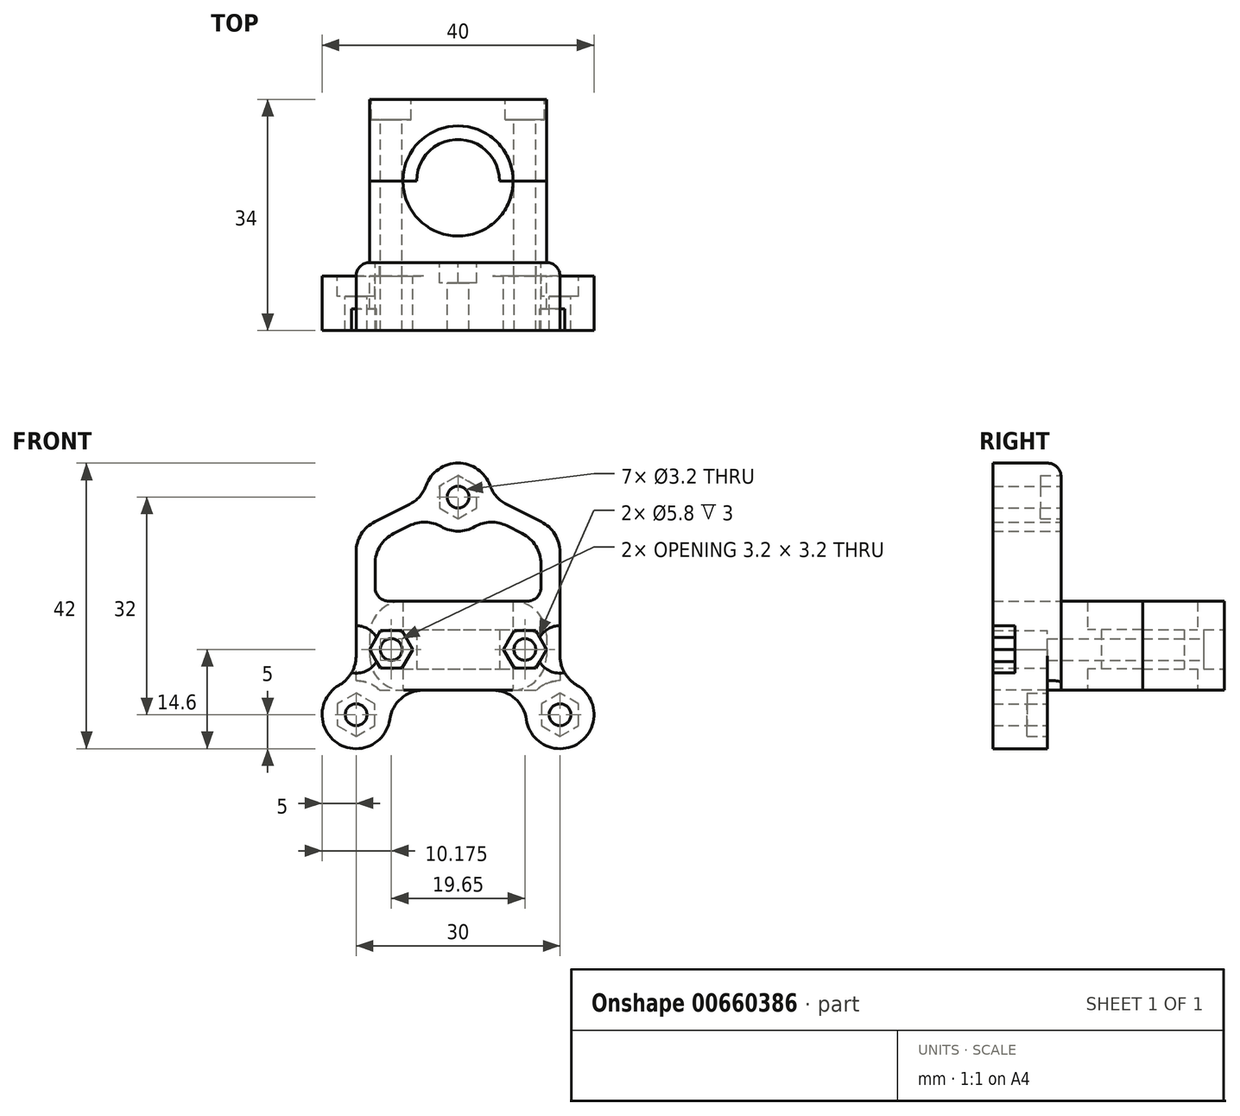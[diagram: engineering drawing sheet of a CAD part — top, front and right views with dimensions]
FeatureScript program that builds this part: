
annotation { "Feature Type Name" : "Feature", "Feature Type Description" : "" }
export const myFeature = defineFeature(function(context is Context, id is Id, definition is map)
    precondition{}
    {
        {
            var Q0;
            Q0=qCreatedBy(makeId("Front.planeOp"),FACE);
            var sketch = newSketch(context, id + "F0", { "sketchPlane" : qUnion([Q0])});
            skCircle(sketch, "E0", {"center": v(0, 0) * mm, "radius": 1.6 * mm});
            skCircle(sketch, "E1", {"center": v(-15, -32) * mm, "radius": 1.6 * mm});
            skCircle(sketch, "E2", {"center": v(15, -32) * mm, "radius": 1.6 * mm});
            skCircle(sketch, "E3", {"center": v(0, 0) * mm, "radius": 5 * mm});
            skCircle(sketch, "E4", {"center": v(-15, -32) * mm, "radius": 5 * mm});
            skCircle(sketch, "E5", {"center": v(15, -32) * mm, "radius": 5 * mm});
            skLineSegment(sketch, "E6", {"start": v(-34.89, -28.4) * mm, "end": v(34.55, -28.4) * mm, "construction": true});
            skLineSegment(sketch, "E7", {"start": v(-36.38, -22.4) * mm, "end": v(39.22, -22.4) * mm, "construction": true});
            skLineSegment(sketch, "E8", {"start": v(-25.23, 0) * mm, "end": v(32.74, 0) * mm, "construction": true});
            skPoint(sketch, "E9", {"position": v(0, -5) * mm});
            skLineSegment(sketch, "E10", {"start": v(-5, 0) * mm, "end": v(-15, -5) * mm});
            skLineSegment(sketch, "E11", {"start": v(5, 0) * mm, "end": v(15, -5) * mm});
            skCircle(sketch, "E12.cCircle", {"center": v(-9.82, -22.4) * mm, "radius": 2.75 * mm, "construction": true});
            skLineSegment(sketch, "E12.0", {"start": v(-8.24, -25.15) * mm, "end": v(-11.41, -25.15) * mm});
            skLineSegment(sketch, "E12.1", {"start": v(-11.41, -25.15) * mm, "end": v(-13, -22.4) * mm});
            skLineSegment(sketch, "E12.2", {"start": v(-13, -22.4) * mm, "end": v(-11.41, -19.65) * mm});
            skLineSegment(sketch, "E12.3", {"start": v(-11.41, -19.65) * mm, "end": v(-8.24, -19.65) * mm});
            skLineSegment(sketch, "E12.4", {"start": v(-8.24, -19.65) * mm, "end": v(-6.65, -22.4) * mm});
            skLineSegment(sketch, "E12.5", {"start": v(-6.65, -22.4) * mm, "end": v(-8.24, -25.15) * mm});
            skPoint(sketch, "E12.0.midPoint", {"position": v(0, -22.4) * mm});
            skLineSegment(sketch, "E13", {"start": v(-15, -5) * mm, "end": v(-15, -27) * mm});
            skLineSegment(sketch, "E14", {"start": v(15, -5) * mm, "end": v(15, -27) * mm});
            skLineSegment(sketch, "E15", {"start": v(-11.53, -28.4) * mm, "end": v(11.53, -28.4) * mm});
            skLineSegment(sketch, "E16", {"start": v(-30.83, -32) * mm, "end": v(25.55, -32) * mm, "construction": true});
            skLineSegment(sketch, "E17", {"start": v(-10, -32) * mm, "end": v(-10, -28.4) * mm});
            skLineSegment(sketch, "E18", {"start": v(10, -32) * mm, "end": v(10, -28.4) * mm});
            skLineSegment(sketch, "E19", {"start": v(-12.2, -15.3) * mm, "end": v(12.2, -15.3) * mm});
            skLineSegment(sketch, "E20.0", {"start": v(-4.2, -2.73) * mm, "end": v(-12.2, -6.73) * mm});
            skLineSegment(sketch, "E21.0", {"start": v(4.2, -2.73) * mm, "end": v(12.2, -6.73) * mm});
            skLineSegment(sketch, "E22", {"start": v(-12.2, -6.73) * mm, "end": v(-12.2, -15.3) * mm});
            skLineSegment(sketch, "E23", {"start": v(12.2, -6.73) * mm, "end": v(12.2, -15.3) * mm});
            skCircle(sketch, "E24.cCircle", {"center": v(9.82, -22.4) * mm, "radius": 2.75 * mm, "construction": true});
            skLineSegment(sketch, "E24.0", {"start": v(11.41, -25.15) * mm, "end": v(8.24, -25.15) * mm});
            skLineSegment(sketch, "E24.1", {"start": v(8.24, -25.15) * mm, "end": v(6.65, -22.4) * mm});
            skLineSegment(sketch, "E24.2", {"start": v(6.65, -22.4) * mm, "end": v(8.24, -19.65) * mm});
            skLineSegment(sketch, "E24.3", {"start": v(8.24, -19.65) * mm, "end": v(11.41, -19.65) * mm});
            skLineSegment(sketch, "E24.4", {"start": v(11.41, -19.65) * mm, "end": v(13, -22.4) * mm});
            skLineSegment(sketch, "E24.5", {"start": v(13, -22.4) * mm, "end": v(11.41, -25.15) * mm});
            skCircle(sketch, "E25", {"center": v(-15, -22.4) * mm, "radius": 3.5 * mm});
            skCircle(sketch, "E26", {"center": v(15, -22.4) * mm, "radius": 3.5 * mm});
            skLineSegment(sketch, "E27.bottom", {"start": v(-3.5, -14.5) * mm, "end": v(3.5, -14.5) * mm, "construction": true});
            skLineSegment(sketch, "E27.top", {"start": v(-3.5, -15.7) * mm, "end": v(3.5, -15.7) * mm, "construction": true});
            skLineSegment(sketch, "E27.left", {"start": v(-3.5, -14.5) * mm, "end": v(-3.5, -15.7) * mm, "construction": true});
            skLineSegment(sketch, "E27.right", {"start": v(3.5, -14.5) * mm, "end": v(3.5, -15.7) * mm, "construction": true});
            skPoint(sketch, "E28", {"position": v(0, -14.5) * mm});
            skLineSegment(sketch, "E29.bottom", {"start": v(-8, -15.7) * mm, "end": v(8, -15.7) * mm, "construction": true});
            skLineSegment(sketch, "E29.top", {"start": v(-8, -19.4) * mm, "end": v(8, -19.4) * mm, "construction": true});
            skLineSegment(sketch, "E29.left", {"start": v(-8, -15.7) * mm, "end": v(-8, -19.4) * mm, "construction": true});
            skLineSegment(sketch, "E29.right", {"start": v(8, -15.7) * mm, "end": v(8, -19.4) * mm, "construction": true});
            skLineSegment(sketch, "E30.bottom", {"start": v(-8, -25.4) * mm, "end": v(8, -25.4) * mm, "construction": true});
            skLineSegment(sketch, "E30.top", {"start": v(-8, -28.4) * mm, "end": v(8, -28.4) * mm, "construction": true});
            skLineSegment(sketch, "E30.left", {"start": v(-8, -25.4) * mm, "end": v(-8, -28.4) * mm, "construction": true});
            skLineSegment(sketch, "E30.right", {"start": v(8, -25.4) * mm, "end": v(8, -28.4) * mm, "construction": true});
            skLineSegment(sketch, "E31.bottom", {"start": v(-6, -19.4) * mm, "end": v(6, -19.4) * mm, "construction": true});
            skLineSegment(sketch, "E31.top", {"start": v(-6, -25.4) * mm, "end": v(6, -25.4) * mm, "construction": true});
            skLineSegment(sketch, "E31.left", {"start": v(-6, -19.4) * mm, "end": v(-6, -25.4) * mm, "construction": true});
            skLineSegment(sketch, "E31.right", {"start": v(6, -19.4) * mm, "end": v(6, -25.4) * mm, "construction": true});
            skLineSegment(sketch, "E32.bottom", {"start": v(-5, -28.4) * mm, "end": v(5, -28.4) * mm, "construction": true});
            skLineSegment(sketch, "E33", {"start": v(0, -14.5) * mm, "end": v(0, -28.4) * mm, "construction": true});
            skLineSegment(sketch, "E34", {"start": v(-13, -2.8) * mm, "end": v(-13, -40.8) * mm, "construction": true});
            skLineSegment(sketch, "E35", {"start": v(13, -2.8) * mm, "end": v(13, -40.8) * mm, "construction": true});
            skPoint(sketch, "E36", {"position": v(-8, -23.4) * mm});
            skPoint(sketch, "E37", {"position": v(8, -23.4) * mm});
            skArc(sketch, "E38", {"start": v(-8, -15.3) * mm, "mid": v(-11.54, -16.76) * mm, "end": v(-13, -20.3) * mm, "construction": true});
            skArc(sketch, "E39", {"start": v(8, -15.3) * mm, "mid": v(11.54, -16.76) * mm, "end": v(13, -20.3) * mm, "construction": true});
            skArc(sketch, "E40", {"start": v(-8, -28.4) * mm, "mid": v(-11.54, -26.94) * mm, "end": v(-13, -23.4) * mm, "construction": true});
            skArc(sketch, "E41", {"start": v(8, -28.4) * mm, "mid": v(11.54, -26.94) * mm, "end": v(13, -23.4) * mm, "construction": true});
            skSolve(sketch);
        }
        {
            var Q0;
            {var subQ18=sQuery(id+"F0.wireOp",EDGE,"E10");Q0=makeQuery(id+"F0.imprint","IMPRINT",FACE,{"disambiguationData":[TD([[makeQuery(id+"F0.imprint","IMPRINT",EDGE,{"derivedFrom":subQ18}),1.0]])]});}
            var Q1;
            Q1=makeQuery(id+"F0.imprint","IMPRINT",FACE,{"disambiguationData":[TD([[makeQuery(id+"F0.imprint","IMPRINT",EDGE,{"derivedFrom":sQuery(id+"F0.wireOp",EDGE,"E1")}),-1.0]])]});
            var Q2;
            {var subQ3=sQuery(id+"F0.wireOp",EDGE,"E17");Q2=makeQuery(id+"F0.imprint","IMPRINT",FACE,{"disambiguationData":[TD([[makeQuery(id+"F0.imprint","IMPRINT",EDGE,{"derivedFrom":subQ3}),1.0]])]});}
            var Q3;
            Q3=makeQuery(id+"F0.imprint","IMPRINT",FACE,{"disambiguationData":[TD([[makeQuery(id+"F0.imprint","IMPRINT",EDGE,{"derivedFrom":sQuery(id+"F0.wireOp",EDGE,"E2")}),-1.0]])]});
            var Q4;
            {var subQ3=sQuery(id+"F0.wireOp",EDGE,"E18");Q4=makeQuery(id+"F0.imprint","IMPRINT",FACE,{"disambiguationData":[TD([[makeQuery(id+"F0.imprint","IMPRINT",EDGE,{"derivedFrom":subQ3}),-1.0]])]});}
            var Q5;
            Q5=makeQuery(id+"F0.imprint","IMPRINT",FACE,{"disambiguationData":[TD([[makeQuery(id+"F0.imprint","IMPRINT",EDGE,{"derivedFrom":sQuery(id+"F0.wireOp",EDGE,"E0")}),-1.0]])]});
            extrude(context, id + "F1", {"entities" : qUnion([Q0, Q1, Q2, Q3, Q4, Q5]), "oppositeDirection" : true, "depth" : -22 * mm, "offsetDistance" : 25 * mm, "hasSecondDirection" : true, "secondDirectionOppositeDirection" : true, "secondDirectionDepth" : -18.8 * mm});
        }
        {
            var Q0;
            Q0=makeQuery(id+"F0.imprint","IMPRINT",FACE,{"disambiguationData":[TD([[makeQuery(id+"F0.imprint","IMPRINT",EDGE,{"derivedFrom":sQuery(id+"F0.wireOp",EDGE,"E1")}),-1.0]])]});
            var Q1;
            {var subQ3=sQuery(id+"F0.wireOp",EDGE,"E17");Q1=makeQuery(id+"F0.imprint","IMPRINT",FACE,{"disambiguationData":[TD([[makeQuery(id+"F0.imprint","IMPRINT",EDGE,{"derivedFrom":subQ3}),1.0]])]});}
            var Q2;
            {var subQ4=sQuery(id+"F0.wireOp",EDGE,"E12.2");var subQ5=sQuery(id+"F0.wireOp",EDGE,"E12.1");var subQ6=makeQuery(id+"F0.imprint","INTERSECT",VERTEX,{"derivedFrom":[subQ5,subQ4]});Q2=makeQuery(id+"F0.imprint","IMPRINT",FACE,{"disambiguationData":[TD([[makeQuery(id+"F0.imprint","IMPRINT",EDGE,{"disambiguationData":[TD([[subQ6,1.0]])],"derivedFrom":subQ5}),1.0]])]});}
            var Q3;
            Q3=makeQuery(id+"F0.imprint","IMPRINT",FACE,{"disambiguationData":[TD([[makeQuery(id+"F0.imprint","IMPRINT",EDGE,{"derivedFrom":sQuery(id+"F0.wireOp",EDGE,"E0")}),-1.0]])]});
            var Q4;
            {var subQ0=sQuery(id+"F0.wireOp",EDGE,"E26");var subQ1=sQuery(id+"F0.wireOp",EDGE,"E14");var subQ2=makeQuery(id+"F0.imprint","INTERSECT",VERTEX,{"disambiguationData":[OD(0.0)],"derivedFrom":[subQ1,subQ0]});Q4=makeQuery(id+"F0.imprint","IMPRINT",FACE,{"disambiguationData":[TD([[makeQuery(id+"F0.imprint","IMPRINT",EDGE,{"disambiguationData":[TD([[subQ2,-1.0]])],"derivedFrom":subQ1}),-1.0]])]});}
            var Q5;
            {var subQ16=sQuery(id+"F0.wireOp",EDGE,"E10");Q5=makeQuery(id+"F0.imprint","IMPRINT",FACE,{"disambiguationData":[TD([[makeQuery(id+"F0.imprint","IMPRINT",EDGE,{"derivedFrom":subQ16}),1.0]])]});}
            var Q6;
            {var subQ3=sQuery(id+"F0.wireOp",EDGE,"E18");Q6=makeQuery(id+"F0.imprint","IMPRINT",FACE,{"disambiguationData":[TD([[makeQuery(id+"F0.imprint","IMPRINT",EDGE,{"derivedFrom":subQ3}),-1.0]])]});}
            var Q7;
            Q7=makeQuery(id+"F0.imprint","IMPRINT",FACE,{"disambiguationData":[TD([[makeQuery(id+"F0.imprint","IMPRINT",EDGE,{"derivedFrom":sQuery(id+"F0.wireOp",EDGE,"E2")}),-1.0]])]});
            extrude(context, id + "F2", {"entities" : qUnion([Q0, Q1, Q2, Q3, Q4, Q5, Q6, Q7]), "operationType" : NewBodyOperationType.ADD, "oppositeDirection" : true, "depth" : -18.8 * mm, "offsetDistance" : 25 * mm, "hasSecondDirection" : true, "secondDirectionOppositeDirection" : true, "secondDirectionDepth" : -14 * mm});
        }
        {
            var Q0;
            {var subQ16=sQuery(id+"F0.wireOp",EDGE,"E10");Q0=makeQuery(id+"F0.imprint","IMPRINT",FACE,{"disambiguationData":[TD([[makeQuery(id+"F0.imprint","IMPRINT",EDGE,{"derivedFrom":subQ16}),1.0]])]});}
            var Q1;
            {var subQ5=sQuery(id+"F0.wireOp",EDGE,"E12.0");Q1=makeQuery(id+"F0.imprint","IMPRINT",FACE,{"disambiguationData":[TD([[makeQuery(id+"F0.imprint","IMPRINT",EDGE,{"derivedFrom":subQ5}),-1.0]])]});}
            var Q2;
            {var subQ0=sQuery(id+"F0.wireOp",EDGE,"E12.2");var subQ1=sQuery(id+"F0.wireOp",EDGE,"E12.1");var subQ2=makeQuery(id+"F0.imprint","INTERSECT",VERTEX,{"derivedFrom":[subQ1,subQ0]});Q2=makeQuery(id+"F0.imprint","IMPRINT",FACE,{"disambiguationData":[TD([[makeQuery(id+"F0.imprint","IMPRINT",EDGE,{"disambiguationData":[TD([[subQ2,1.0]])],"derivedFrom":subQ1}),-1.0]])]});}
            var Q3;
            {var subQ4=sQuery(id+"F0.wireOp",EDGE,"E12.2");var subQ5=sQuery(id+"F0.wireOp",EDGE,"E12.1");var subQ6=makeQuery(id+"F0.imprint","INTERSECT",VERTEX,{"derivedFrom":[subQ5,subQ4]});Q3=makeQuery(id+"F0.imprint","IMPRINT",FACE,{"disambiguationData":[TD([[makeQuery(id+"F0.imprint","IMPRINT",EDGE,{"disambiguationData":[TD([[subQ6,1.0]])],"derivedFrom":subQ5}),1.0]])]});}
            var Q4;
            {var subQ6=sQuery(id+"F0.wireOp",EDGE,"E24.0");Q4=makeQuery(id+"F0.imprint","IMPRINT",FACE,{"disambiguationData":[TD([[makeQuery(id+"F0.imprint","IMPRINT",EDGE,{"derivedFrom":subQ6}),-1.0]])]});}
            var Q5;
            {var subQ0=sQuery(id+"F0.wireOp",EDGE,"E26");var subQ1=sQuery(id+"F0.wireOp",EDGE,"E14");var subQ2=makeQuery(id+"F0.imprint","INTERSECT",VERTEX,{"disambiguationData":[OD(0.0)],"derivedFrom":[subQ1,subQ0]});Q5=makeQuery(id+"F0.imprint","IMPRINT",FACE,{"disambiguationData":[TD([[makeQuery(id+"F0.imprint","IMPRINT",EDGE,{"disambiguationData":[TD([[subQ2,-1.0]])],"derivedFrom":subQ1}),-1.0]])]});}
            var Q6;
            {var subQ0=sQuery(id+"F0.wireOp",EDGE,"E24.5");var subQ1=sQuery(id+"F0.wireOp",EDGE,"E24.4");var subQ2=makeQuery(id+"F0.imprint","INTERSECT",VERTEX,{"derivedFrom":[subQ1,subQ0]});Q6=makeQuery(id+"F0.imprint","IMPRINT",FACE,{"disambiguationData":[TD([[makeQuery(id+"F0.imprint","IMPRINT",EDGE,{"disambiguationData":[TD([[subQ2,1.0]])],"derivedFrom":subQ1}),-1.0]])]});}
            var Q7;
            Q7=makeQuery(id+"F0.imprint","IMPRINT",FACE,{"disambiguationData":[TD([[makeQuery(id+"F0.imprint","IMPRINT",EDGE,{"derivedFrom":sQuery(id+"F0.wireOp",EDGE,"E0")}),-1.0]])]});
            extrude(context, id + "F3", {"entities" : qUnion([Q0, Q1, Q2, Q3, Q4, Q5, Q6, Q7]), "operationType" : NewBodyOperationType.ADD, "oppositeDirection" : true, "depth" : -14 * mm, "offsetDistance" : 25 * mm, "hasSecondDirection" : true, "secondDirectionOppositeDirection" : true, "secondDirectionDepth" : -12 * mm});
        }
        {
            var Q0;
            Q0=qCreatedBy(makeId("Front.planeOp"),FACE);
            var sketch = newSketch(context, id + "F4", { "sketchPlane" : qUnion([Q0])});
            skPoint(sketch, "E42.0.midPoint", {"position": v(0, -22.4) * mm});
            skArc(sketch, "E43", {"start": v(-8, -15.3) * mm, "mid": v(-11.54, -16.76) * mm, "end": v(-13, -20.3) * mm});
            skArc(sketch, "E44", {"start": v(8, -15.3) * mm, "mid": v(11.54, -16.76) * mm, "end": v(13, -20.3) * mm});
            skArc(sketch, "E45", {"start": v(-8, -28.4) * mm, "mid": v(-11.54, -26.94) * mm, "end": v(-13, -23.4) * mm});
            skArc(sketch, "E46", {"start": v(8, -28.4) * mm, "mid": v(11.54, -26.94) * mm, "end": v(13, -23.4) * mm});
            skLineSegment(sketch, "E47", {"start": v(-13, -20.3) * mm, "end": v(-13, -23.4) * mm});
            skLineSegment(sketch, "E48", {"start": v(-8, -15.3) * mm, "end": v(8, -15.3) * mm});
            skLineSegment(sketch, "E49", {"start": v(13, -20.3) * mm, "end": v(13, -23.4) * mm});
            skLineSegment(sketch, "E50", {"start": v(8, -28.4) * mm, "end": v(-8, -28.4) * mm});
            skPoint(sketch, "E51", {"position": v(-9.82, -22.4) * mm});
            skPoint(sketch, "E52", {"position": v(9.83, -22.4) * mm});
            skSolve(sketch);
        }
        {
            var Q0;
            Q0 = qSketchRegion(id + "F4", true);
            extrude(context, id + "F5", {"entities" : qUnion([Q0]), "operationType" : NewBodyOperationType.ADD, "depth" : 12 * mm, "offsetDistance" : 25 * mm});
        }
        {
            var Q0;
            Q0 = qSketchRegion(id + "F4", true);
            extrude(context, id + "F6", {"entities" : qUnion([Q0]), "oppositeDirection" : true, "depth" : 12 * mm, "offsetDistance" : 25 * mm});
        }
        {
            var Q0;
            Q0=qCreatedBy(makeId("Front.planeOp"),FACE);
            var sketch = newSketch(context, id + "F7", { "sketchPlane" : qUnion([Q0])});
            skLineSegment(sketch, "E53.bottom", {"start": v(-3.5, -14.5) * mm, "end": v(3.5, -14.5) * mm});
            skLineSegment(sketch, "E53.top", {"start": v(-3.5, -15.7) * mm, "end": v(3.5, -15.7) * mm});
            skLineSegment(sketch, "E53.left", {"start": v(-3.5, -14.5) * mm, "end": v(-3.5, -15.7) * mm});
            skLineSegment(sketch, "E53.right", {"start": v(3.5, -14.5) * mm, "end": v(3.5, -15.7) * mm});
            skLineSegment(sketch, "E54.bottom", {"start": v(-8, -15.7) * mm, "end": v(8, -15.7) * mm});
            skLineSegment(sketch, "E54.top", {"start": v(-8, -19.4) * mm, "end": v(8, -19.4) * mm});
            skLineSegment(sketch, "E54.left", {"start": v(-8, -15.7) * mm, "end": v(-8, -19.4) * mm});
            skLineSegment(sketch, "E54.right", {"start": v(8, -15.7) * mm, "end": v(8, -19.4) * mm});
            skLineSegment(sketch, "E55.bottom", {"start": v(-8, -25.4) * mm, "end": v(8, -25.4) * mm});
            skLineSegment(sketch, "E55.top", {"start": v(-8, -28.4) * mm, "end": v(8, -28.4) * mm});
            skLineSegment(sketch, "E55.left", {"start": v(-8, -25.4) * mm, "end": v(-8, -28.4) * mm});
            skLineSegment(sketch, "E55.right", {"start": v(8, -25.4) * mm, "end": v(8, -28.4) * mm});
            skLineSegment(sketch, "E56.bottom", {"start": v(-6, -19.4) * mm, "end": v(6, -19.4) * mm});
            skLineSegment(sketch, "E56.top", {"start": v(-6, -25.4) * mm, "end": v(6, -25.4) * mm});
            skLineSegment(sketch, "E56.left", {"start": v(-6, -19.4) * mm, "end": v(-6, -25.4) * mm});
            skLineSegment(sketch, "E56.right", {"start": v(6, -19.4) * mm, "end": v(6, -25.4) * mm});
            skLineSegment(sketch, "E57.bottom", {"start": v(-5, -28.4) * mm, "end": v(5, -28.4) * mm});
            skLineSegment(sketch, "E58", {"start": v(0, -10.7) * mm, "end": v(0, -28.4) * mm});
            skPoint(sketch, "E59", {"position": v(0, -22.4) * mm});
            skLineSegment(sketch, "E60.bottom", {"start": v(-8, -10.7) * mm, "end": v(8, -10.7) * mm});
            skLineSegment(sketch, "E61", {"start": v(8, -10.7) * mm, "end": v(8, -15.7) * mm});
            skLineSegment(sketch, "E62", {"start": v(-8, -10.7) * mm, "end": v(-8, -15.7) * mm});
            skSolve(sketch);
        }
        {
            var Q0;
            {var subQ0=sQuery(id+"F7.wireOp",EDGE,"E53.right");Q0=makeQuery(id+"F7.imprint","IMPRINT",FACE,{"disambiguationData":[TD([[makeQuery(id+"F7.imprint","IMPRINT",EDGE,{"derivedFrom":subQ0}),-1.0]])]});}
            var Q1;
            {var subQ0=sQuery(id+"F7.wireOp",EDGE,"E54.right");Q1=makeQuery(id+"F7.imprint","IMPRINT",FACE,{"disambiguationData":[TD([[makeQuery(id+"F7.imprint","IMPRINT",EDGE,{"derivedFrom":subQ0}),-1.0]])]});}
            var Q2;
            {var subQ1=sQuery(id+"F7.wireOp",EDGE,"E53.right");Q2=makeQuery(id+"F7.imprint","IMPRINT",FACE,{"disambiguationData":[TD([[makeQuery(id+"F7.imprint","IMPRINT",EDGE,{"derivedFrom":subQ1}),1.0]])]});}
            var Q3;
            {var subQ0=sQuery(id+"F7.wireOp",EDGE,"E56.right");Q3=makeQuery(id+"F7.imprint","IMPRINT",FACE,{"disambiguationData":[TD([[makeQuery(id+"F7.imprint","IMPRINT",EDGE,{"derivedFrom":subQ0}),-1.0]])]});}
            var Q4;
            {var subQ5=sQuery(id+"F7.wireOp",EDGE,"E55.right");Q4=makeQuery(id+"F7.imprint","IMPRINT",FACE,{"disambiguationData":[TD([[makeQuery(id+"F7.imprint","IMPRINT",EDGE,{"derivedFrom":subQ5}),-1.0]])]});}
            var Q5;
            Q5=sQuery(id+"F7.wireOp",EDGE,"E58");
            revolve(context, id + "F8", {"entities" : qUnion([Q0, Q1, Q2, Q3, Q4]), "axis" : qUnion([Q5]), "revolveType" : RevolveType.FULL, "oppositeDirection" : true});
        }
        {
            var Q0;
            {var subQ0=sQuery(id+"F0.wireOp",EDGE,"E14");var subQ1=sQuery(id+"F0.wireOp",EDGE,"E2");var subQ2=sQuery(id+"F0.wireOp",EDGE,"E15");var subQ3=sQuery(id+"F0.wireOp",EDGE,"E5");var subQ4=sQuery(id+"F0.wireOp",EDGE,"E18");var subQ5=sQuery(id+"F0.wireOp",EDGE,"E11");Q0=makeQuery(id+"F3.boolean.opBoolean","SPLIT",FACE,{"disambiguationData":[TD([makeQuery(id+"F1.opExtrude","SWEPT_FACE",FACE,{"disambiguationData":[OSD([subQ1])]})])],"derivedFrom":makeQuery(id+"F2.opExtrude","CAP_FACE",FACE,{"disambiguationData":[OSD([sQuery(id+"F0.wireOp",EDGE,"E0"),sQuery(id+"F0.wireOp",EDGE,"E1"),subQ1,sQuery(id+"F0.wireOp",EDGE,"E3"),sQuery(id+"F0.wireOp",EDGE,"E4"),subQ3,sQuery(id+"F0.wireOp",EDGE,"E10"),subQ5,sQuery(id+"F0.wireOp",EDGE,"E12.0"),sQuery(id+"F0.wireOp",EDGE,"E12.1"),sQuery(id+"F0.wireOp",EDGE,"E12.2"),sQuery(id+"F0.wireOp",EDGE,"E12.3"),sQuery(id+"F0.wireOp",EDGE,"E12.4"),sQuery(id+"F0.wireOp",EDGE,"E12.5"),sQuery(id+"F0.wireOp",EDGE,"E13"),subQ0,subQ2,sQuery(id+"F0.wireOp",EDGE,"E17"),subQ4,sQuery(id+"F0.wireOp",EDGE,"E19"),sQuery(id+"F0.wireOp",EDGE,"E20.0"),sQuery(id+"F0.wireOp",EDGE,"E21.0"),sQuery(id+"F0.wireOp",EDGE,"E22"),sQuery(id+"F0.wireOp",EDGE,"E23"),sQuery(id+"F0.wireOp",EDGE,"E24.0"),sQuery(id+"F0.wireOp",EDGE,"E24.1"),sQuery(id+"F0.wireOp",EDGE,"E24.2"),sQuery(id+"F0.wireOp",EDGE,"E24.3"),sQuery(id+"F0.wireOp",EDGE,"E24.4"),sQuery(id+"F0.wireOp",EDGE,"E24.5")])],"isStart":true})});}
            var sketch = newSketch(context, id + "F9", { "sketchPlane" : qUnion([Q0])});
            skCircle(sketch, "E63.cCircle", {"center": v(-15, -32) * mm, "radius": 2.75 * mm, "construction": true});
            skLineSegment(sketch, "E63.0", {"start": v(-12.25, -30.41) * mm, "end": v(-12.25, -33.59) * mm});
            skLineSegment(sketch, "E63.1", {"start": v(-12.25, -33.59) * mm, "end": v(-15, -35.18) * mm});
            skLineSegment(sketch, "E63.2", {"start": v(-15, -35.18) * mm, "end": v(-17.75, -33.59) * mm});
            skLineSegment(sketch, "E63.3", {"start": v(-17.75, -33.59) * mm, "end": v(-17.75, -30.41) * mm});
            skLineSegment(sketch, "E63.4", {"start": v(-17.75, -30.41) * mm, "end": v(-15, -28.82) * mm});
            skLineSegment(sketch, "E63.5", {"start": v(-15, -28.82) * mm, "end": v(-12.25, -30.41) * mm});
            skPoint(sketch, "E63.0.midPoint", {"position": v(-12.25, -32) * mm});
            skSolve(sketch);
        }
        {
            var Q0;
            Q0=makeQuery(id+"F9.imprint","IMPRINT",FACE,{"disambiguationData":[TD([[makeQuery(id+"F9.imprint","IMPRINT",EDGE,{"derivedFrom":makeQuery(id+"F2.opExtrude","CAP_EDGE",EDGE,{"disambiguationData":[OSD([sQuery(id+"F0.wireOp",EDGE,"E2")])],"isStart":true})}),-1.0]])]});
            var Q1;
            Q1=makeQuery(id+"F9.imprint","IMPRINT",FACE,{"disambiguationData":[TD([[makeQuery(id+"F9.imprint","IMPRINT",EDGE,{"derivedFrom":sQuery(id+"F9.wireOp",EDGE,"E63.0")}),-1.0]])]});
            extrude(context, id + "F10", {"entities" : qUnion([Q0, Q1]), "operationType" : NewBodyOperationType.REMOVE, "oppositeDirection" : true, "depth" : 3 * mm, "offsetDistance" : 25 * mm});
        }
        {
            var Q0;
            {var subQ0=sQuery(id+"F0.wireOp",EDGE,"E15");var subQ1=sQuery(id+"F0.wireOp",EDGE,"E4");var subQ2=sQuery(id+"F0.wireOp",EDGE,"E17");var subQ3=sQuery(id+"F0.wireOp",EDGE,"E13");var subQ4=sQuery(id+"F0.wireOp",EDGE,"E1");var subQ6=sQuery(id+"F0.wireOp",EDGE,"E10");Q0=makeQuery(id+"F3.boolean.opBoolean","SPLIT",FACE,{"disambiguationData":[TD([makeQuery(id+"F1.opExtrude","SWEPT_FACE",FACE,{"disambiguationData":[OSD([subQ4])]})])],"derivedFrom":makeQuery(id+"F2.opExtrude","CAP_FACE",FACE,{"disambiguationData":[OSD([sQuery(id+"F0.wireOp",EDGE,"E0"),subQ4,sQuery(id+"F0.wireOp",EDGE,"E2"),sQuery(id+"F0.wireOp",EDGE,"E3"),subQ1,sQuery(id+"F0.wireOp",EDGE,"E5"),subQ6,sQuery(id+"F0.wireOp",EDGE,"E11"),sQuery(id+"F0.wireOp",EDGE,"E12.0"),sQuery(id+"F0.wireOp",EDGE,"E12.1"),sQuery(id+"F0.wireOp",EDGE,"E12.2"),sQuery(id+"F0.wireOp",EDGE,"E12.3"),sQuery(id+"F0.wireOp",EDGE,"E12.4"),sQuery(id+"F0.wireOp",EDGE,"E12.5"),subQ3,sQuery(id+"F0.wireOp",EDGE,"E14"),subQ0,subQ2,sQuery(id+"F0.wireOp",EDGE,"E18"),sQuery(id+"F0.wireOp",EDGE,"E19"),sQuery(id+"F0.wireOp",EDGE,"E20.0"),sQuery(id+"F0.wireOp",EDGE,"E21.0"),sQuery(id+"F0.wireOp",EDGE,"E22"),sQuery(id+"F0.wireOp",EDGE,"E23"),sQuery(id+"F0.wireOp",EDGE,"E24.0"),sQuery(id+"F0.wireOp",EDGE,"E24.1"),sQuery(id+"F0.wireOp",EDGE,"E24.2"),sQuery(id+"F0.wireOp",EDGE,"E24.3"),sQuery(id+"F0.wireOp",EDGE,"E24.4"),sQuery(id+"F0.wireOp",EDGE,"E24.5")])],"isStart":true})});}
            var sketch = newSketch(context, id + "F11", { "sketchPlane" : qUnion([Q0])});
            skCircle(sketch, "E64.cCircle", {"center": v(15, -32) * mm, "radius": 2.75 * mm, "construction": true});
            skLineSegment(sketch, "E64.0", {"start": v(17.75, -30.41) * mm, "end": v(17.75, -33.59) * mm});
            skLineSegment(sketch, "E64.1", {"start": v(17.75, -33.59) * mm, "end": v(15, -35.18) * mm});
            skLineSegment(sketch, "E64.2", {"start": v(15, -35.18) * mm, "end": v(12.25, -33.59) * mm});
            skLineSegment(sketch, "E64.3", {"start": v(12.25, -33.59) * mm, "end": v(12.25, -30.41) * mm});
            skLineSegment(sketch, "E64.4", {"start": v(12.25, -30.41) * mm, "end": v(15, -28.82) * mm});
            skLineSegment(sketch, "E64.5", {"start": v(15, -28.82) * mm, "end": v(17.75, -30.41) * mm});
            skPoint(sketch, "E64.0.midPoint", {"position": v(17.75, -32) * mm});
            skSolve(sketch);
        }
        {
            var Q0;
            Q0=makeQuery(id+"F11.imprint","IMPRINT",FACE,{"disambiguationData":[TD([[makeQuery(id+"F11.imprint","IMPRINT",EDGE,{"derivedFrom":sQuery(id+"F11.wireOp",EDGE,"E64.0")}),-1.0]])]});
            extrude(context, id + "F12", {"entities" : qUnion([Q0]), "operationType" : NewBodyOperationType.REMOVE, "oppositeDirection" : true, "depth" : 3 * mm, "offsetDistance" : 25 * mm});
        }
        {
            var Q0;
            Q0=makeQuery(id+"F3.opExtrude","CAP_FACE",FACE,{"disambiguationData":[OSD([sQuery(id+"F0.wireOp",EDGE,"E0"),sQuery(id+"F0.wireOp",EDGE,"E3"),sQuery(id+"F0.wireOp",EDGE,"E4"),sQuery(id+"F0.wireOp",EDGE,"E5"),sQuery(id+"F0.wireOp",EDGE,"E10"),sQuery(id+"F0.wireOp",EDGE,"E11"),sQuery(id+"F0.wireOp",EDGE,"E13"),sQuery(id+"F0.wireOp",EDGE,"E14"),sQuery(id+"F0.wireOp",EDGE,"E15"),sQuery(id+"F0.wireOp",EDGE,"E19"),sQuery(id+"F0.wireOp",EDGE,"E20.0"),sQuery(id+"F0.wireOp",EDGE,"E21.0"),sQuery(id+"F0.wireOp",EDGE,"E22"),sQuery(id+"F0.wireOp",EDGE,"E23")])],"isStart":true});
            var sketch = newSketch(context, id + "F13", { "sketchPlane" : qUnion([Q0])});
            skCircle(sketch, "E65.cCircle", {"center": v(0, 0) * mm, "radius": 2.75 * mm, "construction": true});
            skLineSegment(sketch, "E65.0", {"start": v(2.75, 1.59) * mm, "end": v(2.75, -1.59) * mm});
            skLineSegment(sketch, "E65.1", {"start": v(2.75, -1.59) * mm, "end": v(0, -3.18) * mm});
            skLineSegment(sketch, "E65.2", {"start": v(0, -3.18) * mm, "end": v(-2.75, -1.59) * mm});
            skLineSegment(sketch, "E65.3", {"start": v(-2.75, -1.59) * mm, "end": v(-2.75, 1.59) * mm});
            skLineSegment(sketch, "E65.4", {"start": v(-2.75, 1.59) * mm, "end": v(0, 3.18) * mm});
            skLineSegment(sketch, "E65.5", {"start": v(0, 3.18) * mm, "end": v(2.75, 1.59) * mm});
            skPoint(sketch, "E65.0.midPoint", {"position": v(2.75, 0) * mm});
            skSolve(sketch);
        }
        {
            var Q0;
            Q0 = qSketchRegion(id + "F13", true);
            extrude(context, id + "F14", {"entities" : qUnion([Q0]), "operationType" : NewBodyOperationType.REMOVE, "oppositeDirection" : true, "depth" : 3 * mm, "offsetDistance" : 25 * mm});
        }
        {
            var Q0;
            Q0=makeQuery(id+"F8.opRevolve","SWEPT_BODY",BODY,{"disambiguationData":[OSD([sQuery(id+"F7.wireOp",EDGE,"E54.top"),sQuery(id+"F7.wireOp",EDGE,"E54.right"),sQuery(id+"F7.wireOp",EDGE,"E55.bottom"),sQuery(id+"F7.wireOp",EDGE,"E55.top"),sQuery(id+"F7.wireOp",EDGE,"E55.right"),sQuery(id+"F7.wireOp",EDGE,"E56.right"),sQuery(id+"F7.wireOp",EDGE,"E57.bottom"),sQuery(id+"F7.wireOp",EDGE,"E58"),sQuery(id+"F7.wireOp",EDGE,"E60.bottom"),sQuery(id+"F7.wireOp",EDGE,"E61")])]});
            var Q1;
            Q1=makeQuery(id+"F6.opExtrude","SWEPT_BODY",BODY,{"disambiguationData":[OSD([sQuery(id+"F4.wireOp",EDGE,"E43"),sQuery(id+"F4.wireOp",EDGE,"E44"),sQuery(id+"F4.wireOp",EDGE,"E45"),sQuery(id+"F4.wireOp",EDGE,"E46"),sQuery(id+"F4.wireOp",EDGE,"E47"),sQuery(id+"F4.wireOp",EDGE,"E48"),sQuery(id+"F4.wireOp",EDGE,"E49"),sQuery(id+"F4.wireOp",EDGE,"E50")])]});
            booleanBodies(context, id + "F15", {"operationType" : BooleanOperationType.SUBTRACTION, "tools" : qUnion([Q0]), "targets" : qUnion([Q1]), "offset" : true, "offsetAll" : true, "offsetDistance" : 0.1 * mm, "keepTools" : true});
        }
        {
            var Q0;
            Q0=makeQuery(id+"F8.opRevolve","SWEPT_BODY",BODY,{"disambiguationData":[OSD([sQuery(id+"F7.wireOp",EDGE,"E54.top"),sQuery(id+"F7.wireOp",EDGE,"E54.right"),sQuery(id+"F7.wireOp",EDGE,"E55.bottom"),sQuery(id+"F7.wireOp",EDGE,"E55.top"),sQuery(id+"F7.wireOp",EDGE,"E55.right"),sQuery(id+"F7.wireOp",EDGE,"E56.right"),sQuery(id+"F7.wireOp",EDGE,"E57.bottom"),sQuery(id+"F7.wireOp",EDGE,"E58"),sQuery(id+"F7.wireOp",EDGE,"E60.bottom"),sQuery(id+"F7.wireOp",EDGE,"E61")])]});
            var Q1;
            Q1=makeQuery(id+"F1.opExtrude","SWEPT_BODY",BODY,{"disambiguationData":[OSD([sQuery(id+"F0.wireOp",EDGE,"E0"),sQuery(id+"F0.wireOp",EDGE,"E1"),sQuery(id+"F0.wireOp",EDGE,"E2"),sQuery(id+"F0.wireOp",EDGE,"E3"),sQuery(id+"F0.wireOp",EDGE,"E4"),sQuery(id+"F0.wireOp",EDGE,"E5"),sQuery(id+"F0.wireOp",EDGE,"E10"),sQuery(id+"F0.wireOp",EDGE,"E11"),sQuery(id+"F0.wireOp",EDGE,"E12.0"),sQuery(id+"F0.wireOp",EDGE,"E12.1"),sQuery(id+"F0.wireOp",EDGE,"E12.2"),sQuery(id+"F0.wireOp",EDGE,"E12.3"),sQuery(id+"F0.wireOp",EDGE,"E12.4"),sQuery(id+"F0.wireOp",EDGE,"E12.5"),sQuery(id+"F0.wireOp",EDGE,"E13"),sQuery(id+"F0.wireOp",EDGE,"E14"),sQuery(id+"F0.wireOp",EDGE,"E15"),sQuery(id+"F0.wireOp",EDGE,"E17"),sQuery(id+"F0.wireOp",EDGE,"E18"),sQuery(id+"F0.wireOp",EDGE,"E19"),sQuery(id+"F0.wireOp",EDGE,"E20.0"),sQuery(id+"F0.wireOp",EDGE,"E21.0"),sQuery(id+"F0.wireOp",EDGE,"E22"),sQuery(id+"F0.wireOp",EDGE,"E23"),sQuery(id+"F0.wireOp",EDGE,"E24.0"),sQuery(id+"F0.wireOp",EDGE,"E24.1"),sQuery(id+"F0.wireOp",EDGE,"E24.2"),sQuery(id+"F0.wireOp",EDGE,"E24.3"),sQuery(id+"F0.wireOp",EDGE,"E24.4"),sQuery(id+"F0.wireOp",EDGE,"E24.5"),sQuery(id+"F0.wireOp",EDGE,"E25"),sQuery(id+"F0.wireOp",EDGE,"E26")])]});
            booleanBodies(context, id + "F16", {"operationType" : BooleanOperationType.SUBTRACTION, "tools" : qUnion([Q0]), "targets" : qUnion([Q1]), "offset" : true, "offsetAll" : true, "offsetDistance" : 0.1 * mm});
        }
        {
            var Q0;
            Q0=sQuery(id+"F0.wireOp",VERTEX,"E24.cCircle.center");
            var Q1;
            Q1=sQuery(id+"F0.wireOp",VERTEX,"E12.cCircle.center");
            var Q2;
            Q2=makeQuery(id+"F1.opExtrude","SWEPT_BODY",BODY,{"disambiguationData":[OSD([sQuery(id+"F0.wireOp",EDGE,"E0"),sQuery(id+"F0.wireOp",EDGE,"E1"),sQuery(id+"F0.wireOp",EDGE,"E2"),sQuery(id+"F0.wireOp",EDGE,"E3"),sQuery(id+"F0.wireOp",EDGE,"E4"),sQuery(id+"F0.wireOp",EDGE,"E5"),sQuery(id+"F0.wireOp",EDGE,"E10"),sQuery(id+"F0.wireOp",EDGE,"E11"),sQuery(id+"F0.wireOp",EDGE,"E12.0"),sQuery(id+"F0.wireOp",EDGE,"E12.1"),sQuery(id+"F0.wireOp",EDGE,"E12.2"),sQuery(id+"F0.wireOp",EDGE,"E12.3"),sQuery(id+"F0.wireOp",EDGE,"E12.4"),sQuery(id+"F0.wireOp",EDGE,"E12.5"),sQuery(id+"F0.wireOp",EDGE,"E13"),sQuery(id+"F0.wireOp",EDGE,"E14"),sQuery(id+"F0.wireOp",EDGE,"E15"),sQuery(id+"F0.wireOp",EDGE,"E17"),sQuery(id+"F0.wireOp",EDGE,"E18"),sQuery(id+"F0.wireOp",EDGE,"E19"),sQuery(id+"F0.wireOp",EDGE,"E20.0"),sQuery(id+"F0.wireOp",EDGE,"E21.0"),sQuery(id+"F0.wireOp",EDGE,"E22"),sQuery(id+"F0.wireOp",EDGE,"E23"),sQuery(id+"F0.wireOp",EDGE,"E24.0"),sQuery(id+"F0.wireOp",EDGE,"E24.1"),sQuery(id+"F0.wireOp",EDGE,"E24.2"),sQuery(id+"F0.wireOp",EDGE,"E24.3"),sQuery(id+"F0.wireOp",EDGE,"E24.4"),sQuery(id+"F0.wireOp",EDGE,"E24.5"),sQuery(id+"F0.wireOp",EDGE,"E25"),sQuery(id+"F0.wireOp",EDGE,"E26")])]});
            hole(context, id + "F17", {"style" : HoleStyle.SIMPLE, "endStyle" : HoleEndStyle.THROUGH, "oppositeDirection" : true, "holeDiameter" : 3.2 * mm, "majorDiameter" : 5 * mm, "isTappedThrough" : true, "tappedDepth" : 12 * mm, "tapClearance" : 3, "locations" : qUnion([Q0, Q1]), "scope" : qUnion([Q2])});
        }
        {
            var Q0;
            {var subQ0=sQuery(id+"F0.wireOp",EDGE,"E10");var subQ1=sQuery(id+"F0.wireOp",EDGE,"E3");Q0=makeQuery(id+"F3.boolean.opBoolean","MERGE",EDGE,{"derivedFrom":[makeQuery(id+"F2.boolean.opBoolean","MERGE",EDGE,{"derivedFrom":[makeQuery(id+"F1.opExtrude","SWEPT_EDGE",EDGE,{"disambiguationData":[OSD([subQ1,subQ0])]}),makeQuery(id+"F2.opExtrude","SWEPT_EDGE",EDGE,{"disambiguationData":[OSD([subQ1,subQ0])]})]}),makeQuery(id+"F3.opExtrude","SWEPT_EDGE",EDGE,{"disambiguationData":[OSD([subQ1,subQ0])]})]});}
            var Q1;
            {var subQ0=sQuery(id+"F0.wireOp",EDGE,"E13");var subQ1=sQuery(id+"F0.wireOp",EDGE,"E10");Q1=makeQuery(id+"F3.boolean.opBoolean","MERGE",EDGE,{"derivedFrom":[makeQuery(id+"F2.boolean.opBoolean","MERGE",EDGE,{"derivedFrom":[makeQuery(id+"F1.opExtrude","SWEPT_EDGE",EDGE,{"disambiguationData":[OSD([subQ1,subQ0])]}),makeQuery(id+"F2.opExtrude","SWEPT_EDGE",EDGE,{"disambiguationData":[OSD([subQ1,subQ0])]})]}),makeQuery(id+"F3.opExtrude","SWEPT_EDGE",EDGE,{"disambiguationData":[OSD([subQ1,subQ0])]})]});}
            var Q2;
            {var subQ0=sQuery(id+"F0.wireOp",EDGE,"E11");var subQ1=sQuery(id+"F0.wireOp",EDGE,"E3");Q2=makeQuery(id+"F3.boolean.opBoolean","MERGE",EDGE,{"derivedFrom":[makeQuery(id+"F2.boolean.opBoolean","MERGE",EDGE,{"derivedFrom":[makeQuery(id+"F1.opExtrude","SWEPT_EDGE",EDGE,{"disambiguationData":[OSD([subQ1,subQ0])]}),makeQuery(id+"F2.opExtrude","SWEPT_EDGE",EDGE,{"disambiguationData":[OSD([subQ1,subQ0])]})]}),makeQuery(id+"F3.opExtrude","SWEPT_EDGE",EDGE,{"disambiguationData":[OSD([subQ1,subQ0])]})]});}
            var Q3;
            {var subQ0=sQuery(id+"F0.wireOp",EDGE,"E14");var subQ1=sQuery(id+"F0.wireOp",EDGE,"E11");Q3=makeQuery(id+"F3.boolean.opBoolean","MERGE",EDGE,{"derivedFrom":[makeQuery(id+"F2.boolean.opBoolean","MERGE",EDGE,{"derivedFrom":[makeQuery(id+"F1.opExtrude","SWEPT_EDGE",EDGE,{"disambiguationData":[OSD([subQ1,subQ0])]}),makeQuery(id+"F2.opExtrude","SWEPT_EDGE",EDGE,{"disambiguationData":[OSD([subQ1,subQ0])]})]}),makeQuery(id+"F3.opExtrude","SWEPT_EDGE",EDGE,{"disambiguationData":[OSD([subQ1,subQ0])]})]});}
            var Q4;
            {var subQ0=sQuery(id+"F0.wireOp",EDGE,"E14");var subQ1=sQuery(id+"F0.wireOp",EDGE,"E5");Q4=makeQuery(id+"F2.boolean.opBoolean","MERGE",EDGE,{"derivedFrom":[makeQuery(id+"F1.opExtrude","SWEPT_EDGE",EDGE,{"disambiguationData":[OSD([subQ1,subQ0])]}),makeQuery(id+"F2.opExtrude","SWEPT_EDGE",EDGE,{"disambiguationData":[OSD([subQ1,subQ0])]})]});}
            var Q5;
            {var subQ0=sQuery(id+"F0.wireOp",EDGE,"E13");var subQ1=sQuery(id+"F0.wireOp",EDGE,"E4");Q5=makeQuery(id+"F2.boolean.opBoolean","MERGE",EDGE,{"derivedFrom":[makeQuery(id+"F1.opExtrude","SWEPT_EDGE",EDGE,{"disambiguationData":[OSD([subQ1,subQ0])]}),makeQuery(id+"F2.opExtrude","SWEPT_EDGE",EDGE,{"disambiguationData":[OSD([subQ1,subQ0])]})]});}
            var Q6;
            {var subQ0=sQuery(id+"F0.wireOp",EDGE,"E18");var subQ1=sQuery(id+"F0.wireOp",EDGE,"E15");Q6=makeQuery(id+"F2.boolean.opBoolean","MERGE",EDGE,{"derivedFrom":[makeQuery(id+"F1.opExtrude","SWEPT_EDGE",EDGE,{"disambiguationData":[OSD([subQ1,subQ0])]}),makeQuery(id+"F2.opExtrude","SWEPT_EDGE",EDGE,{"disambiguationData":[OSD([subQ1,subQ0])]})]});}
            var Q7;
            {var subQ0=sQuery(id+"F0.wireOp",EDGE,"E17");var subQ1=sQuery(id+"F0.wireOp",EDGE,"E15");Q7=makeQuery(id+"F2.boolean.opBoolean","MERGE",EDGE,{"derivedFrom":[makeQuery(id+"F1.opExtrude","SWEPT_EDGE",EDGE,{"disambiguationData":[OSD([subQ1,subQ0])]}),makeQuery(id+"F2.opExtrude","SWEPT_EDGE",EDGE,{"disambiguationData":[OSD([subQ1,subQ0])]})]});}
            var Q8;
            {var subQ0=sQuery(id+"F0.wireOp",EDGE,"E23");var subQ1=sQuery(id+"F0.wireOp",EDGE,"E21.0");Q8=makeQuery(id+"F3.boolean.opBoolean","MERGE",EDGE,{"derivedFrom":[makeQuery(id+"F2.boolean.opBoolean","MERGE",EDGE,{"derivedFrom":[makeQuery(id+"F1.opExtrude","SWEPT_EDGE",EDGE,{"disambiguationData":[OSD([subQ1,subQ0])]}),makeQuery(id+"F2.opExtrude","SWEPT_EDGE",EDGE,{"disambiguationData":[OSD([subQ1,subQ0])]})]}),makeQuery(id+"F3.opExtrude","SWEPT_EDGE",EDGE,{"disambiguationData":[OSD([subQ1,subQ0])]})]});}
            var Q9;
            {var subQ0=sQuery(id+"F0.wireOp",EDGE,"E21.0");var subQ1=sQuery(id+"F0.wireOp",EDGE,"E3");Q9=makeQuery(id+"F3.boolean.opBoolean","MERGE",EDGE,{"derivedFrom":[makeQuery(id+"F2.boolean.opBoolean","MERGE",EDGE,{"derivedFrom":[makeQuery(id+"F1.opExtrude","SWEPT_EDGE",EDGE,{"disambiguationData":[OSD([subQ1,subQ0])]}),makeQuery(id+"F2.opExtrude","SWEPT_EDGE",EDGE,{"disambiguationData":[OSD([subQ1,subQ0])]})]}),makeQuery(id+"F3.opExtrude","SWEPT_EDGE",EDGE,{"disambiguationData":[OSD([subQ1,subQ0])]})]});}
            var Q10;
            {var subQ0=sQuery(id+"F0.wireOp",EDGE,"E20.0");var subQ1=sQuery(id+"F0.wireOp",EDGE,"E3");Q10=makeQuery(id+"F3.boolean.opBoolean","MERGE",EDGE,{"derivedFrom":[makeQuery(id+"F2.boolean.opBoolean","MERGE",EDGE,{"derivedFrom":[makeQuery(id+"F1.opExtrude","SWEPT_EDGE",EDGE,{"disambiguationData":[OSD([subQ1,subQ0])]}),makeQuery(id+"F2.opExtrude","SWEPT_EDGE",EDGE,{"disambiguationData":[OSD([subQ1,subQ0])]})]}),makeQuery(id+"F3.opExtrude","SWEPT_EDGE",EDGE,{"disambiguationData":[OSD([subQ1,subQ0])]})]});}
            var Q11;
            {var subQ0=sQuery(id+"F0.wireOp",EDGE,"E22");var subQ1=sQuery(id+"F0.wireOp",EDGE,"E20.0");Q11=makeQuery(id+"F3.boolean.opBoolean","MERGE",EDGE,{"derivedFrom":[makeQuery(id+"F2.boolean.opBoolean","MERGE",EDGE,{"derivedFrom":[makeQuery(id+"F1.opExtrude","SWEPT_EDGE",EDGE,{"disambiguationData":[OSD([subQ1,subQ0])]}),makeQuery(id+"F2.opExtrude","SWEPT_EDGE",EDGE,{"disambiguationData":[OSD([subQ1,subQ0])]})]}),makeQuery(id+"F3.opExtrude","SWEPT_EDGE",EDGE,{"disambiguationData":[OSD([subQ1,subQ0])]})]});}
            fillet(context, id + "F18", {"entities" : qUnion([Q0, Q1, Q2, Q3, Q4, Q5, Q6, Q7, Q8, Q9, Q10, Q11]), "radius" : 5 * mm, "tangentPropagation" : true, "allowEdgeOverflow" : false});
        }
        {
            var Q0;
            Q0=makeQuery(id+"F3.opExtrude","CAP_EDGE",EDGE,{"disambiguationData":[OSD([sQuery(id+"F0.wireOp",EDGE,"E14")])],"isStart":true});
            fillet(context, id + "F19", {"entities" : qUnion([Q0]), "radius" : 2 * mm, "tangentPropagation" : true, "allowEdgeOverflow" : false});
        }
        {
            var Q0;
            {var subQ0=sQuery(id+"F0.wireOp",EDGE,"E22");var subQ1=sQuery(id+"F0.wireOp",EDGE,"E19");Q0=makeQuery(id+"F3.boolean.opBoolean","MERGE",EDGE,{"derivedFrom":[makeQuery(id+"F2.boolean.opBoolean","MERGE",EDGE,{"derivedFrom":[makeQuery(id+"F1.opExtrude","SWEPT_EDGE",EDGE,{"disambiguationData":[OSD([subQ1,subQ0])]}),makeQuery(id+"F2.opExtrude","SWEPT_EDGE",EDGE,{"disambiguationData":[OSD([subQ1,subQ0])]})]}),makeQuery(id+"F3.opExtrude","SWEPT_EDGE",EDGE,{"disambiguationData":[OSD([subQ1,subQ0])]})]});}
            var Q1;
            {var subQ0=sQuery(id+"F0.wireOp",EDGE,"E23");var subQ1=sQuery(id+"F0.wireOp",EDGE,"E19");Q1=makeQuery(id+"F3.boolean.opBoolean","MERGE",EDGE,{"derivedFrom":[makeQuery(id+"F2.boolean.opBoolean","MERGE",EDGE,{"derivedFrom":[makeQuery(id+"F1.opExtrude","SWEPT_EDGE",EDGE,{"disambiguationData":[OSD([subQ1,subQ0])]}),makeQuery(id+"F2.opExtrude","SWEPT_EDGE",EDGE,{"disambiguationData":[OSD([subQ1,subQ0])]})]}),makeQuery(id+"F3.opExtrude","SWEPT_EDGE",EDGE,{"disambiguationData":[OSD([subQ1,subQ0])]})]});}
            fillet(context, id + "F20", {"entities" : qUnion([Q0, Q1]), "radius" : 2 * mm, "tangentPropagation" : true, "allowEdgeOverflow" : false});
        }
        {
            var Q0;
            Q0=makeQuery(id+"F6.opExtrude","CAP_FACE",FACE,{"disambiguationData":[OSD([sQuery(id+"F4.wireOp",EDGE,"E43"),sQuery(id+"F4.wireOp",EDGE,"E44"),sQuery(id+"F4.wireOp",EDGE,"E45"),sQuery(id+"F4.wireOp",EDGE,"E46"),sQuery(id+"F4.wireOp",EDGE,"E47"),sQuery(id+"F4.wireOp",EDGE,"E48"),sQuery(id+"F4.wireOp",EDGE,"E49"),sQuery(id+"F4.wireOp",EDGE,"E50")])],"isStart":false});
            var sketch = newSketch(context, id + "F21", { "sketchPlane" : qUnion([Q0])});
            skPoint(sketch, "E66", {"position": v(9.82, -22.4) * mm});
            skPoint(sketch, "E67", {"position": v(-9.83, -22.4) * mm});
            skSolve(sketch);
        }
        {
            var Q0;
            Q0=sQuery(id+"F21.wireOp",VERTEX,"E67");
            var Q1;
            Q1=sQuery(id+"F21.wireOp",VERTEX,"E66");
            var Q2;
            Q2=makeQuery(id+"F6.opExtrude","SWEPT_BODY",BODY,{"disambiguationData":[OSD([sQuery(id+"F4.wireOp",EDGE,"E43"),sQuery(id+"F4.wireOp",EDGE,"E44"),sQuery(id+"F4.wireOp",EDGE,"E45"),sQuery(id+"F4.wireOp",EDGE,"E46"),sQuery(id+"F4.wireOp",EDGE,"E47"),sQuery(id+"F4.wireOp",EDGE,"E48"),sQuery(id+"F4.wireOp",EDGE,"E49"),sQuery(id+"F4.wireOp",EDGE,"E50")])]});
            hole(context, id + "F22", {"style" : HoleStyle.C_BORE, "endStyle" : HoleEndStyle.THROUGH, "holeDiameter" : 3.2 * mm, "cBoreDiameter" : 5.8 * mm, "cBoreDepth" : 3 * mm, "majorDiameter" : 5 * mm, "isTappedThrough" : true, "tappedDepth" : 12 * mm, "tapClearance" : 3, "locations" : qUnion([Q0, Q1]), "scope" : qUnion([Q2])});
        }
    });
